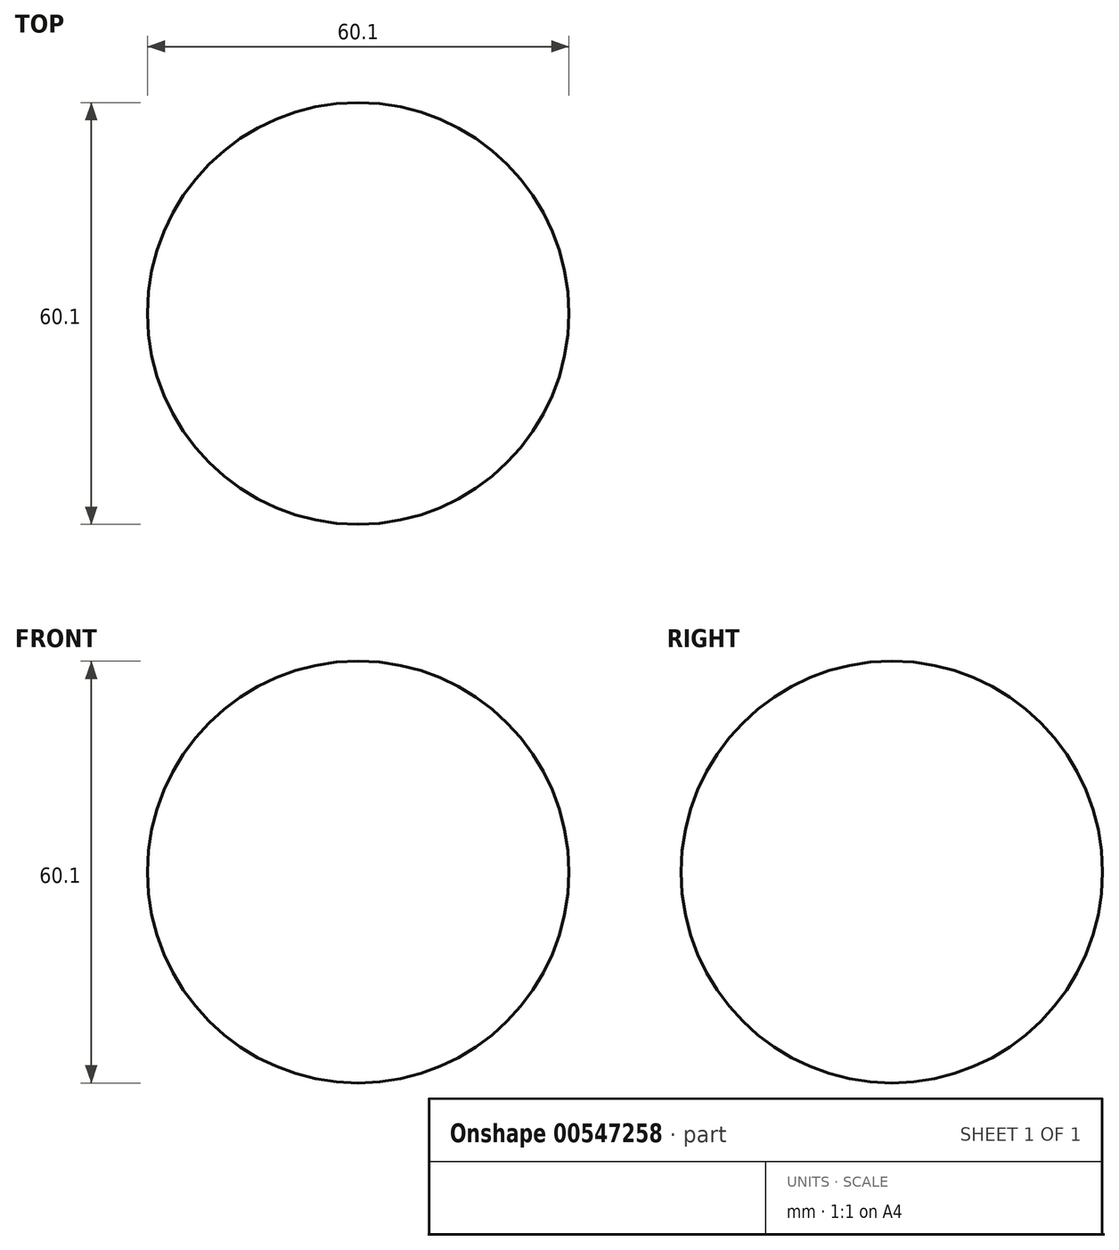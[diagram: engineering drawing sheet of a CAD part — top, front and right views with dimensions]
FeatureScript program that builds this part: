
annotation { "Feature Type Name" : "Feature", "Feature Type Description" : "" }
export const myFeature = defineFeature(function(context is Context, id is Id, definition is map)
    precondition{}
    {
        {
            var Q0;
            Q0=qCreatedBy(makeId("Front.planeOp"),FACE);
            var sketch = newSketch(context, id + "F0", { "sketchPlane" : qUnion([Q0])});
            skArc(sketch, "E0", {"start": v(0, -30.05) * mm, "mid": v(30.05, 0) * mm, "end": v(0, 30.05) * mm});
            skLineSegment(sketch, "E1", {"start": v(0, 30.05) * mm, "end": v(0, -30.05) * mm});
            skSolve(sketch);
        }
        {
            var Q0;
            Q0=qCreatedBy(makeId("Front.planeOp"),FACE);
            var sketch = newSketch(context, id + "F1", { "sketchPlane" : qUnion([Q0])});
            skLineSegment(sketch, "E2", {"start": v(0, 28.9) * mm, "end": v(0, -30.31) * mm});
            skSolve(sketch);
        }
        {
            var Q0;
            Q0 = qSketchRegion(id + "F0", true);
            var Q1;
            Q1=sQuery(id+"F1.wireOp",EDGE,"E2");
            revolve(context, id + "F2", {"entities" : qUnion([Q0]), "axis" : qUnion([Q1]), "revolveType" : RevolveType.FULL});
        }
    });
